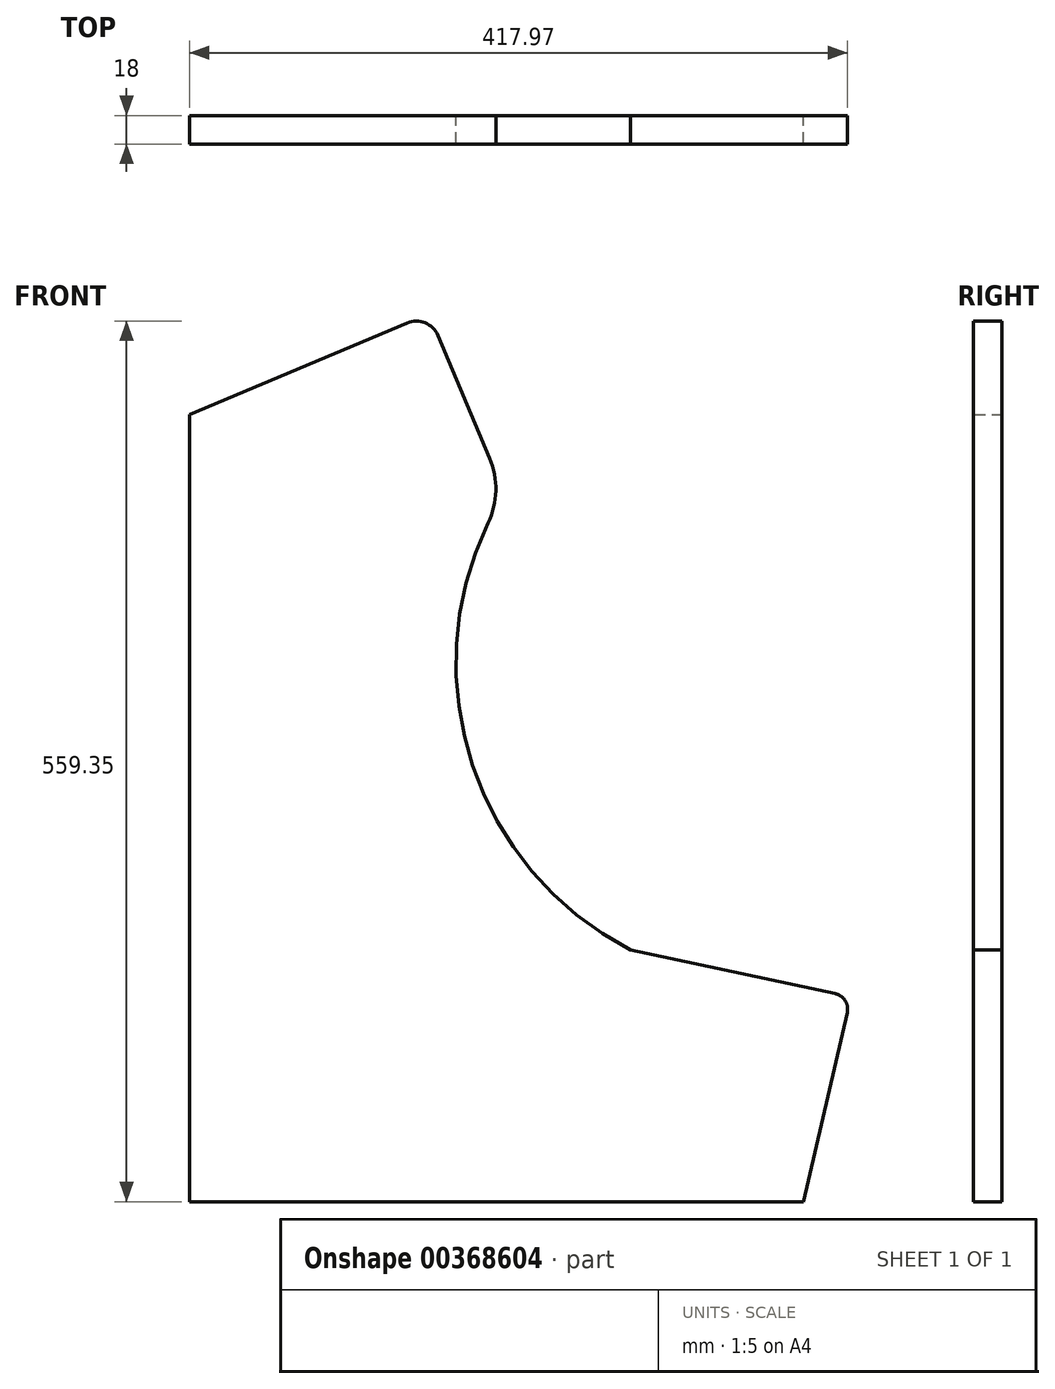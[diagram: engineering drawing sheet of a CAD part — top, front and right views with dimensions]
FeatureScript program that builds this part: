
annotation { "Feature Type Name" : "Feature", "Feature Type Description" : "" }
export const myFeature = defineFeature(function(context is Context, id is Id, definition is map)
    precondition{}
    {
        {
            var Q0;
            Q0=qCreatedBy(makeId("Front.planeOp"),FACE);
            var sketch = newSketch(context, id + "F0", { "sketchPlane" : qUnion([Q0])});
            skLineSegment(sketch, "E0", {"start": v(0, 0) * mm, "end": v(390, 0) * mm});
            skLineSegment(sketch, "E1", {"start": v(390, 0) * mm, "end": v(417.72, 120.1) * mm});
            skLineSegment(sketch, "E2", {"start": v(0, 0) * mm, "end": v(0, 500) * mm});
            skLineSegment(sketch, "E3", {"start": v(410.07, 132.13) * mm, "end": v(280, 160) * mm});
            skLineSegment(sketch, "E4", {"start": v(157.82, 550.18) * mm, "end": v(190.66, 472.2) * mm});
            skLineSegment(sketch, "E5", {"start": v(0, 500) * mm, "end": v(138.18, 558.18) * mm});
            skArc(sketch, "E6", {"start": v(189.61, 431.07) * mm, "mid": v(179.8, 277.2) * mm, "end": v(280, 160) * mm});
            skPoint(sketch, "E7.visualSharp", {"position": v(420, 130) * mm});
            skArc(sketch, "E7.filletArc", {"start": v(417.72, 120.1) * mm, "mid": v(416.4, 127.72) * mm, "end": v(410.07, 132.13) * mm});
            skPoint(sketch, "E8.visualSharp", {"position": v(152, 564) * mm});
            skArc(sketch, "E8.filletArc", {"start": v(157.82, 550.18) * mm, "mid": v(149.66, 558.25) * mm, "end": v(138.18, 558.18) * mm});
            skPoint(sketch, "E9.visualSharp", {"position": v(200, 450) * mm});
            skArc(sketch, "E9.filletArc", {"start": v(189.61, 431.07) * mm, "mid": v(194.56, 451.52) * mm, "end": v(190.66, 472.2) * mm});
            skLineSegment(sketch, "E10", {"start": v(190.66, 472.2) * mm, "end": v(200, 450) * mm, "construction": true});
            skLineSegment(sketch, "E11", {"start": v(200, 450) * mm, "end": v(189.61, 431.07) * mm, "construction": true});
            skSolve(sketch);
        }
        {
            var Q0;
            Q0=makeQuery(id+"F0.imprint","IMPRINT",FACE,{"disambiguationData":[TD([[makeQuery(id+"F0.imprint","IMPRINT",EDGE,{"derivedFrom":sQuery(id+"F0.wireOp",EDGE,"E0")}),1.0]])]});
            extrude(context, id + "F1", {"entities" : qUnion([Q0]), "depth" : 18 * mm});
        }
    });
